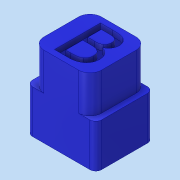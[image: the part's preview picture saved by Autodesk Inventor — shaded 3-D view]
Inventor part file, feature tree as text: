
AUTODESK INVENTOR PART (.ipt)
format: ipt  version: 2018 (Build 220112000, 112)  size: 188,928 bytes
history: native  units: mm
features: sketch x3, extrude x2, fillet x2, other x1, projected_geometry x1
ambient origin geometry x8: Origin, YZ Plane, XZ Plane, XY Plane, X Axis, Y Axis, Z Axis, Center Point
bodies: Volumenkörper1 (feature_tree)
feature tree (9):
  extrude  "Extrusion1"  Depth=10.0mm
  extrude  "Extrusion2"  Depth=10.0mm
  fillet  "Rundung1"  Radius=10.0mm
  fillet  "Rundung2"  Radius=6.5mm
  other  "Prägen1"
  sketch  "Skizze1"  dims[d0=12.0mm d1=10.0mm]
  sketch  "Skizze2"  dims[d2=14.0mm d3=0.0mm d4=10.0mm d5=10.0mm d6=6.5mm d7=0.0mm]
  sketch  "Skizze3"  dims[d8=2.0mm d9=1.0mm d10=1.0mm d11=1.0mm d12=1.0mm d13=3.490659mm]
  projected_geometry  "Projizierte Kontur1"
